# Revit family: Building-ConnessioniIEC309-GEWISS-66IB-PRESE-INTERBLOCCATE-HD_IP66_SENZA_FONDO_24V
name_source: partatom
category: Apparecchi elettrici
units: mm (PartAtom-declared; Revit-internal decimal feet)

## family parameters
Condiviso = Sì
Host = Superficie
Mantenere orientamento annotazione = Sì
Punto di calcolo locali = Sì
Quota connettore circolare = Usa diametro
Taglio con vuoti quando caricato = Sì
Tipo di parte = Normale

## types (1)
- Building-ConnessioniIEC309-GEWISS-66IB-PRESE-INTERBLOCCATE-HD_IP66_SENZA_FONDO_24V
    Catalogo = BUILDING
    Catalogo Serie = 66 IB
    Codice EAN = 8011564184114
    Codice Electrocod = 2222
    Colore = Viola
    Colore: = Viola
    Con fondo = No
    Corpo presa = Light Blue
    Corrente nominale (A) = 16
    Corrente nominale (In) = 16
    Descrizione = PRESA BL.IP66 S.F.2P 160VA TRASF.CBF
    Frequenza = 50 Hz
    Frequenza nominale (Hz) = 50 Hz
    Glow Wire Test = 850 °C
    Glow wire test: = 850 °C
    Grado di protezione = IP66
    IDF = 98e80978-bc6f-4a14-8bf4-1e4813759065
    IDT = 31c4d5ce-9998-4c76-8b01-e5caf3d26d86
    Immagine tipo = R.jpg
    Modello = GW66886
    N. poli = 2P
    Numero di poli = 2P
    Potenza = 160VA
    Potenza nominale = 160VA
    Produttore = GEWISS S.p.A.
    Prospetto di default = 1219 mm
    Protezione = Trasformatore di sicurezza
    Resistenza agli urti = > IK10
    Resistenza agli urti a -20°C = 20J
    SEO = Presa
    Scheda Tecnica = https://www.gewiss.com
    Simbolo presa = PRESAINDSTAGNA : 3P
    Struttura = Grigio RAL - 7035
    Temperatura di funzionamento = -25 ÷ +40 °C
    Temperatura di utilizzo = -25 +40 °C
    Tensione di uscita = 20-25 V
    Termopressione con biglia = 80 °C
    Tipo di impiego = Impieghi gravosi
    Tipo fusibile = Ø 10,3x38 mm
    Tipologia = Verticale
    URL = https://www.gewiss.com
    Versione file RFA = 21.4
    giallo = 0 mm  [stored 0 ft]
    n-poli = 1
    presa = Grigio RAL - 7035
    vetro = Default - Vetro
    volt = 0 V

note: [stored X ft] marks values corroborated as IEEE doubles in the binary element streams (Revit-internal decimal feet)

## geometry (parser evidence)
native form markers: Sweep x5
no freeform markers — native parametric forms only
